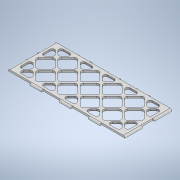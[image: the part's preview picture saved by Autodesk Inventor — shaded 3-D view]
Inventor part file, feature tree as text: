
AUTODESK INVENTOR PART (.ipt)
format: ipt  version: 2020 (Build 240168000, 168)  size: 482,816 bytes
history: native  units: in
note: dims shown in document units (in); Inventor stores cm internally (conversion verified against a paired STEP export)
features: fillet x2, extrude x1, sketch x1
ambient origin geometry x8: Origin, YZ Plane, XZ Plane, XY Plane, X Axis, Y Axis, Z Axis, Center Point
bodies: Solid1 (feature_tree)
feature tree (4):
  extrude  "Extrusion1"  Depth=1.5748in
  fillet  "Fillet1"  Radius=0.9843in
  fillet  "Fillet2"  Radius=0.9843in
  sketch  "Sketch1"  dims[d0=3.937in d1=1.5748in d2=0.9843in d3=0.9843in d4=0.9843in d5=0.9843in d6=0.1969in d7=0.3937in d8=0.0591in d9=0.1969in d10=0.3937in d11=0.0591in d12=0.1969in d13=0.3937in d14=0.0591in d15=0.1969in d16=0.0591in d17=0.3937in d18=0.1969in d19=0.0591in d20=0.3937in d27=0.0984in d28=0.748in d29=0.748in d30=0.748in d31=0.748in d32=0.748in d33=0.0984in d34=0.0394in d35=1.9685in d37=0.748in d38=0.3937in d40=1.0in d42=135.0deg d43=1.5748in d45=0.748in d46=0.3937in d48=1.0in d50=1.9685in d52=0.748in d53=0.3937in d55=1.0in d57=0.3937in d58=0.0591in d59=0.3937in d60=0.0591in d61=0.3937in d62=0.0591in d63=0.0591in d64=0.0in d65=0.0787in d66=0.0591in d44=0.5in]
